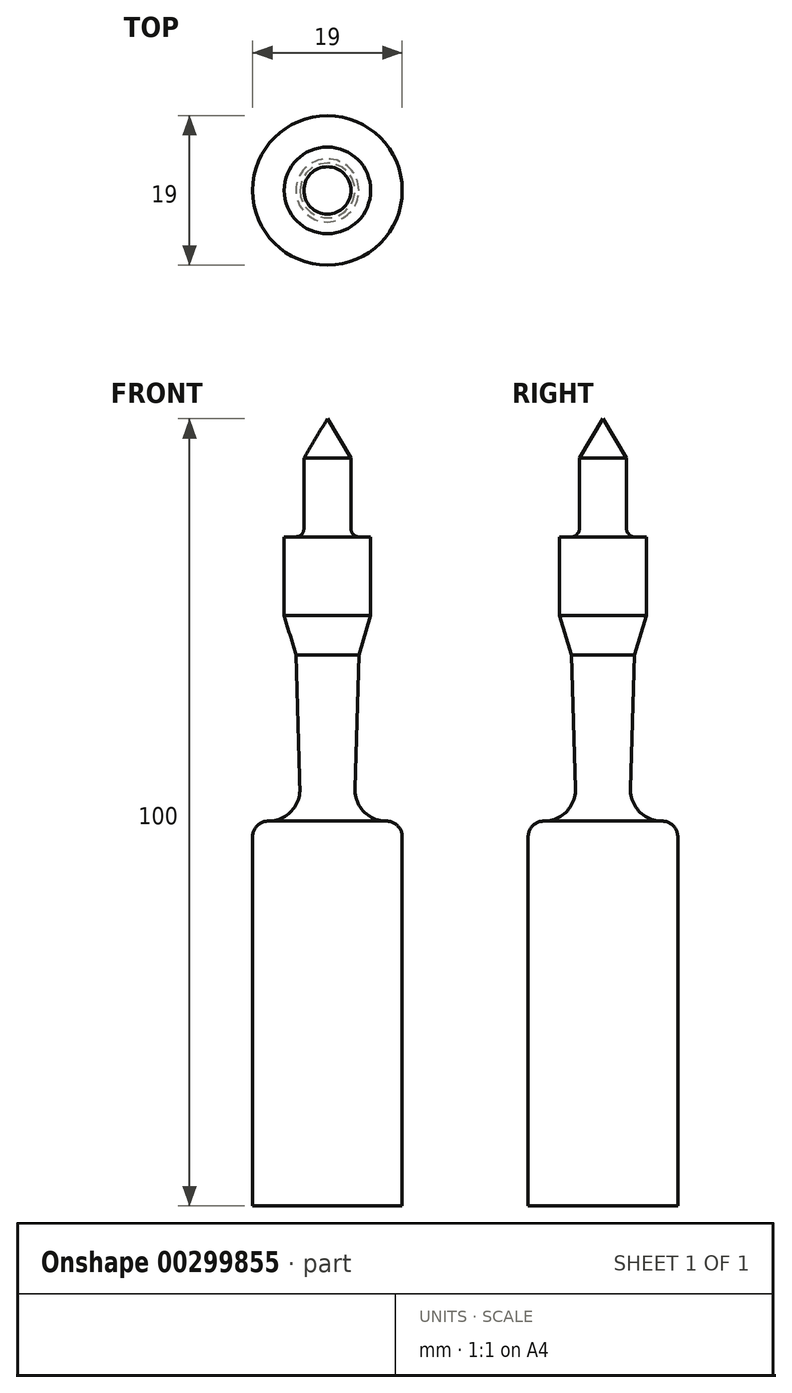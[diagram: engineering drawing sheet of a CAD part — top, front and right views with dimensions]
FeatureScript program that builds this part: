
annotation { "Feature Type Name" : "Feature", "Feature Type Description" : "" }
export const myFeature = defineFeature(function(context is Context, id is Id, definition is map)
    precondition{}
    {
        {
            var Q0;
            Q0=qCreatedBy(makeId("Front.planeOp"),FACE);
            var sketch = newSketch(context, id + "F0", { "sketchPlane" : qUnion([Q0])});
            skLineSegment(sketch, "E0", {"start": v(0, 0) * mm, "end": v(3, -5) * mm});
            skLineSegment(sketch, "E1", {"start": v(3, -5) * mm, "end": v(3, -14) * mm});
            skArc(sketch, "E2", {"start": v(3, -14) * mm, "mid": v(3.3, -14.7) * mm, "end": v(4, -15) * mm});
            skLineSegment(sketch, "E3", {"start": v(4, -15) * mm, "end": v(5.5, -15) * mm});
            skLineSegment(sketch, "E4", {"start": v(5.5, -15) * mm, "end": v(5.5, -25) * mm});
            skLineSegment(sketch, "E5", {"start": v(5.5, -25) * mm, "end": v(4, -30) * mm});
            skLineSegment(sketch, "E6", {"start": v(4, -30) * mm, "end": v(3.5, -47) * mm});
            skArc(sketch, "E7", {"start": v(3.5, -47) * mm, "mid": v(4.63, -49.9) * mm, "end": v(7.5, -51.12) * mm});
            skArc(sketch, "E8", {"start": v(9.5, -53.12) * mm, "mid": v(8.91, -51.7) * mm, "end": v(7.5, -51.12) * mm});
            skLineSegment(sketch, "E9", {"start": v(9.5, -53.12) * mm, "end": v(9.5, -100) * mm});
            skLineSegment(sketch, "E10", {"start": v(9.5, -100) * mm, "end": v(0, -100) * mm});
            skLineSegment(sketch, "E11", {"start": v(0, -100) * mm, "end": v(0, 0) * mm});
            skSolve(sketch);
        }
        {
            var Q0;
            Q0=makeQuery(id+"F0.imprint","IMPRINT",FACE,{"disambiguationData":[TD([[makeQuery(id+"F0.imprint","IMPRINT",EDGE,{"derivedFrom":sQuery(id+"F0.wireOp",EDGE,"E0")}),-1.0]])]});
            var Q1;
            Q1=sQuery(id+"F0.wireOp",EDGE,"E11");
            revolve(context, id + "F1", {"entities" : qUnion([Q0]), "axis" : qUnion([Q1]), "revolveType" : RevolveType.FULL});
        }
    });
